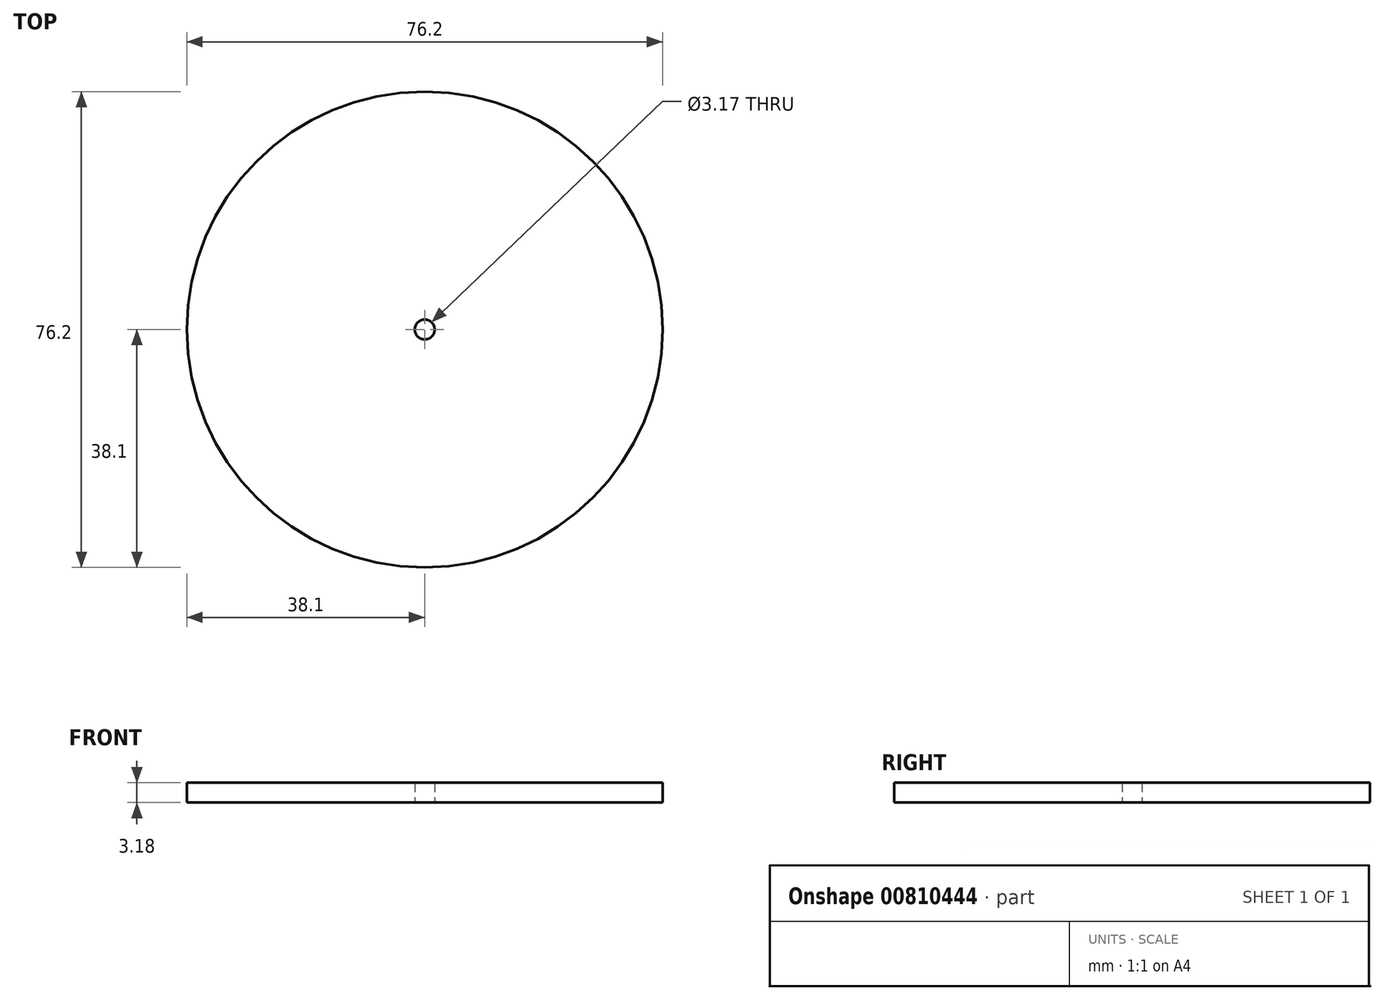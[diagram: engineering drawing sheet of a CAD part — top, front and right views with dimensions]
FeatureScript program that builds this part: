
annotation { "Feature Type Name" : "Feature", "Feature Type Description" : "" }
export const myFeature = defineFeature(function(context is Context, id is Id, definition is map)
    precondition{}
    {
        {
            var Q0;
            Q0=qCreatedBy(makeId("Top.planeOp"),FACE);
            var sketch = newSketch(context, id + "F0", { "sketchPlane" : qUnion([Q0])});
            skCircle(sketch, "E0", {"center": v(0, 0) * mm, "radius": 38.1 * mm});
            skCircle(sketch, "E1", {"center": v(0, 0) * mm, "radius": 1.59 * mm});
            skSolve(sketch);
        }
        {
            var Q0;
            Q0=makeQuery(id+"F0.imprint","IMPRINT",FACE,{"disambiguationData":[TD([[makeQuery(id+"F0.imprint","IMPRINT",EDGE,{"derivedFrom":sQuery(id+"F0.wireOp",EDGE,"E0")}),1.0]])]});
            extrude(context, id + "F1", {"entities" : qUnion([Q0]), "depth" : 3.17 * mm, "offsetDistance" : 25.4 * mm});
        }
        {
            var Q0;
            Q0=makeQuery(id+"F0.imprint","IMPRINT",FACE,{"disambiguationData":[TD([[makeQuery(id+"F0.imprint","IMPRINT",EDGE,{"derivedFrom":sQuery(id+"F0.wireOp",EDGE,"E1")}),1.0]])]});
            extrude(context, id + "F2", {"entities" : qUnion([Q0]), "operationType" : NewBodyOperationType.REMOVE, "oppositeDirection" : true, "depth" : 3.17 * mm, "offsetDistance" : 25.4 * mm});
        }
    });
